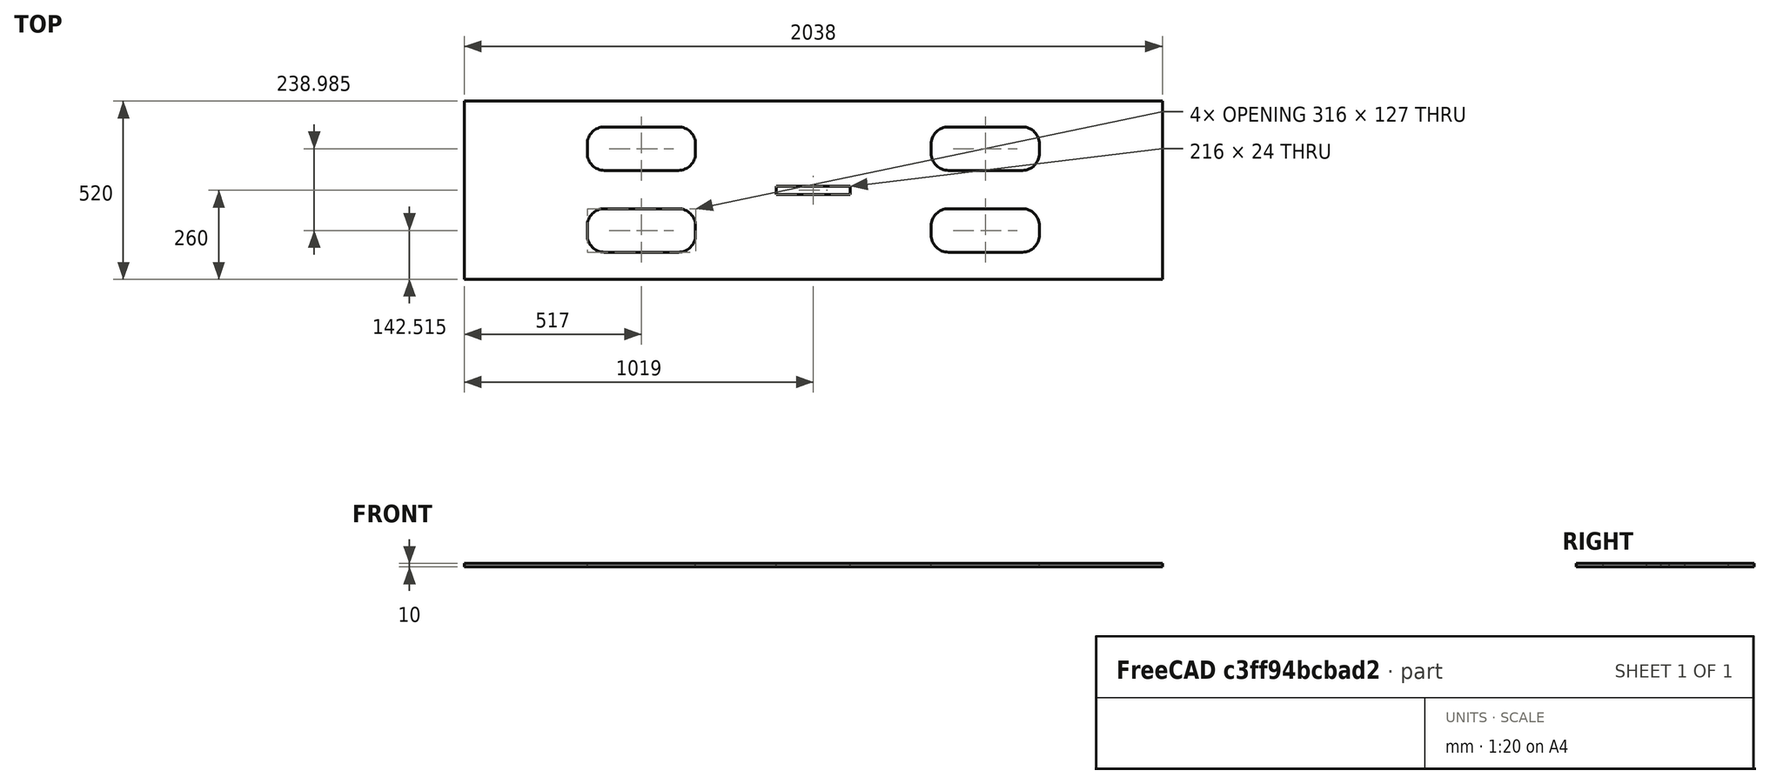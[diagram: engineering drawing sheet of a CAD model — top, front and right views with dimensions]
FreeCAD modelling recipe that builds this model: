
FCSTD DOCUMENT  (FreeCAD 1.0R39319 (Git))
Label: comp20_16mm_plate
License: All rights reserved
LicenseURL: https://en.wikipedia.org/wiki/All_rights_reserved
objects: Sketcher::SketchObject×1, PartDesign::Pad×1, PartDesign::Body×1
note: 6 computed .brp shape members not serialized (recipe doc carries the construction recipe); baked Part::Feature solids carry a one-line shape summary decoded from their .brp

FEATURE [Sketcher::SketchObject] Sketch
  ArcFitTolerance = 1e-06
  AttachmentSupport = -> [XY_Plane]
  FullyConstrained = true
  MakeInternals = false
  MapMode = 5
  sketch-geometry (50):
    g0: LineSegment StartX=0 StartY=0 StartZ=0 EndX=2038 EndY=0 EndZ=0
    g1: LineSegment StartX=2038 StartY=0 StartZ=0 EndX=2038 EndY=520 EndZ=0
    g2: LineSegment StartX=2038 StartY=520 StartZ=0 EndX=0 EndY=520 EndZ=0
    g3: LineSegment StartX=0 StartY=520 StartZ=0 EndX=0 EndY=0 EndZ=0
    g4: LineSegment StartX=359 StartY=395 StartZ=0 EndX=359 EndY=368 EndZ=0
    g5: LineSegment StartX=409 StartY=318 StartZ=0 EndX=625 EndY=318 EndZ=0
    g6: LineSegment StartX=675 StartY=368 StartZ=0 EndX=675 EndY=395 EndZ=0
    g7: LineSegment StartX=625 StartY=445 StartZ=0 EndX=409 EndY=445 EndZ=0
    g8: ArcOfCircle CenterX=409 CenterY=395 CenterZ=0 NormalX=0 NormalY=0 NormalZ=1 AngleXU=0 Radius=50 StartAngle=1.5708 EndAngle=3.14159
    g9: ArcOfCircle CenterX=409 CenterY=368 CenterZ=0 NormalX=0 NormalY=0 NormalZ=1 AngleXU=0 Radius=50 StartAngle=3.14159 EndAngle=4.71239
    g10: ArcOfCircle CenterX=625 CenterY=368 CenterZ=0 NormalX=0 NormalY=0 NormalZ=1 AngleXU=0 Radius=50 StartAngle=4.71239 EndAngle=6.28319
    g11: ArcOfCircle CenterX=625 CenterY=395 CenterZ=0 NormalX=0 NormalY=0 NormalZ=1 AngleXU=0 Radius=50 StartAngle=-1.33e-14 EndAngle=1.5708
    g12: GeomPoint [constr] X=359 Y=445 Z=0
    g13: GeomPoint [constr] X=675 Y=318 Z=0
    g14: LineSegment StartX=1363 StartY=395 StartZ=0 EndX=1363 EndY=368 EndZ=0
    g15: LineSegment StartX=1413 StartY=318 StartZ=0 EndX=1629 EndY=318 EndZ=0
    g16: LineSegment StartX=1679 StartY=368 StartZ=0 EndX=1679 EndY=395 EndZ=0
    g17: LineSegment StartX=1629 StartY=445 StartZ=0 EndX=1413 EndY=445 EndZ=0
    g18: ArcOfCircle CenterX=1413 CenterY=395 CenterZ=0 NormalX=0 NormalY=0 NormalZ=1 AngleXU=0 Radius=50 StartAngle=1.5708 EndAngle=3.14159
    g19: ArcOfCircle CenterX=1413 CenterY=368 CenterZ=0 NormalX=0 NormalY=0 NormalZ=1 AngleXU=0 Radius=50 StartAngle=3.14159 EndAngle=4.71239
    g20: ArcOfCircle CenterX=1629 CenterY=368 CenterZ=0 NormalX=0 NormalY=0 NormalZ=1 AngleXU=0 Radius=50 StartAngle=4.71239 EndAngle=6.28319
    g21: ArcOfCircle CenterX=1629 CenterY=395 CenterZ=0 NormalX=0 NormalY=0 NormalZ=1 AngleXU=0 Radius=50 StartAngle=-1.42e-14 EndAngle=1.5708
    g22: GeomPoint [constr] X=1363 Y=445 Z=0
    g23: GeomPoint [constr] X=1679 Y=318 Z=0
    g24: LineSegment StartX=359 StartY=156.015 StartZ=0 EndX=359 EndY=129.015 EndZ=0
    g25: LineSegment StartX=409 StartY=79.0146 StartZ=0 EndX=625 EndY=79.0146 EndZ=0
    g26: LineSegment StartX=675 StartY=129.015 StartZ=0 EndX=675 EndY=156.015 EndZ=0
    g27: LineSegment StartX=625 StartY=206.015 StartZ=0 EndX=409 EndY=206.015 EndZ=0
    g28: ArcOfCircle CenterX=409 CenterY=156.015 CenterZ=0 NormalX=0 NormalY=0 NormalZ=1 AngleXU=0 Radius=50 StartAngle=1.5708 EndAngle=3.14159
    g29: ArcOfCircle CenterX=409 CenterY=129.015 CenterZ=0 NormalX=0 NormalY=0 NormalZ=1 AngleXU=0 Radius=50 StartAngle=3.14159 EndAngle=4.71239
    g30: ArcOfCircle CenterX=625 CenterY=129.015 CenterZ=0 NormalX=0 NormalY=0 NormalZ=1 AngleXU=0 Radius=50 StartAngle=4.71239 EndAngle=6.28319
    g31: ArcOfCircle CenterX=625 CenterY=156.015 CenterZ=0 NormalX=0 NormalY=0 NormalZ=1 AngleXU=0 Radius=50 StartAngle=1e-16 EndAngle=1.5708
    g32: GeomPoint [constr] X=359 Y=206.015 Z=0
    g33: GeomPoint [constr] X=675 Y=79.0146 Z=0
    g34: LineSegment StartX=1363 StartY=156.015 StartZ=0 EndX=1363 EndY=129.015 EndZ=0
    g35: LineSegment StartX=1413 StartY=79.0146 StartZ=0 EndX=1629 EndY=79.0146 EndZ=0
    g36: LineSegment StartX=1679 StartY=129.015 StartZ=0 EndX=1679 EndY=156.015 EndZ=0
    g37: LineSegment StartX=1629 StartY=206.015 StartZ=0 EndX=1413 EndY=206.015 EndZ=0
    g38: ArcOfCircle CenterX=1413 CenterY=156.015 CenterZ=0 NormalX=0 NormalY=0 NormalZ=1 AngleXU=0 Radius=50 StartAngle=1.5708 EndAngle=3.14159
    g39: ArcOfCircle CenterX=1413 CenterY=129.015 CenterZ=0 NormalX=0 NormalY=0 NormalZ=1 AngleXU=0 Radius=50 StartAngle=3.14159 EndAngle=4.71239
    g40: ArcOfCircle CenterX=1629 CenterY=129.015 CenterZ=0 NormalX=0 NormalY=0 NormalZ=1 AngleXU=0 Radius=50 StartAngle=4.71239 EndAngle=6.28319
    g41: ArcOfCircle CenterX=1629 CenterY=156.015 CenterZ=0 NormalX=0 NormalY=0 NormalZ=1 AngleXU=0 Radius=50 StartAngle=0 EndAngle=1.5708
    g42: GeomPoint [constr] X=1363 Y=206.015 Z=0
    g43: GeomPoint [constr] X=1679 Y=79.0146 Z=0
    g44: LineSegment StartX=911 StartY=272 StartZ=0 EndX=911 EndY=248 EndZ=0
    g45: LineSegment StartX=911 StartY=248 StartZ=0 EndX=1127 EndY=248 EndZ=0
    g46: LineSegment StartX=1127 StartY=248 StartZ=0 EndX=1127 EndY=272 EndZ=0
    g47: LineSegment StartX=1127 StartY=272 StartZ=0 EndX=911 EndY=272 EndZ=0
    g48: LineSegment [constr] StartX=1019 StartY=520 StartZ=0 EndX=1019 EndY=272 EndZ=0
    g49: LineSegment [constr] StartX=1019 StartY=248 StartZ=0 EndX=1019 EndY=0 EndZ=0
  constraints (123):
    c: Coincident(g0,g1)
    c: Coincident(g1,g2)
    c: Coincident(g2,g3)
    c: Coincident(g3,g0)
    c: Horizontal(g0)
    c: Horizontal(g2)
    c: Vertical(g1)
    c: Vertical(g3)
    c: Coincident(g0,g-1)
    c: DistanceX(g2,g2) = 2038
    c: DistanceY(g1,g1) = 520
    c: Tangent(g4,g8) = -1.5708
    c: Tangent(g4,g9) = -1.5708
    c: Tangent(g5,g9) = -1.5708
    c: Tangent(g5,g10) = -1.5708
    c: Tangent(g6,g10) = -1.5708
    c: Tangent(g6,g11) = -1.5708
    c: Tangent(g7,g11) = -1.5708
    c: Tangent(g7,g8) = -1.5708
    c: Vertical(g4)
    c: Vertical(g6)
    c: Horizontal(g5)
    c: Horizontal(g7)
    c: Equal(g8,g9)
    c: Equal(g9,g10)
    c: Equal(g10,g11)
    c: PointOnObject(g12,g4)
    c: PointOnObject(g12,g7)
    c: PointOnObject(g13,g5)
    c: PointOnObject(g13,g6)
    c: Tangent(g14,g18) = -1.5708
    c: Tangent(g14,g19) = -1.5708
    c: Tangent(g15,g19) = -1.5708
    c: Tangent(g15,g20) = -1.5708
    c: Tangent(g16,g20) = -1.5708
    c: Tangent(g16,g21) = -1.5708
    c: Tangent(g17,g21) = -1.5708
    c: Tangent(g17,g18) = -1.5708
    c: Vertical(g14)
    c: Vertical(g16)
    c: Horizontal(g15)
    c: Horizontal(g17)
    c: Equal(g18,g19)
    c: Equal(g19,g20)
    c: Equal(g20,g21)
    c: PointOnObject(g22,g14)
    c: PointOnObject(g22,g17)
    c: PointOnObject(g23,g15)
    c: PointOnObject(g23,g16)
    c: Tangent(g24,g28) = -1.5708
    c: Tangent(g24,g29) = -1.5708
    c: Tangent(g25,g29) = -1.5708
    c: Tangent(g25,g30) = -1.5708
    c: Tangent(g26,g30) = -1.5708
    c: Tangent(g26,g31) = -1.5708
    c: Tangent(g27,g31) = -1.5708
    c: Tangent(g27,g28) = -1.5708
    c: Vertical(g24)
    c: Vertical(g26)
    c: Horizontal(g25)
    c: Horizontal(g27)
    c: Equal(g28,g29)
    c: Equal(g29,g30)
    c: Equal(g30,g31)
    c: PointOnObject(g32,g24)
    c: PointOnObject(g32,g27)
    c: PointOnObject(g33,g25)
    c: PointOnObject(g33,g26)
    c: DistanceX(g7,g7) = 216
    c: Radius(g8) = 50
    c: DistanceY(g6,g6) = 27
    c: Equal(g7,g27)
    c: Equal(g27,g17)
    c: Equal(g8,g28)
    c: Equal(g28,g18)
    c: Equal(g6,g14)
    c: Equal(g14,g26)
    c: Tangent(g34,g38) = -1.5708
    c: Tangent(g34,g39) = -1.5708
    c: Tangent(g35,g39) = -1.5708
    c: Tangent(g35,g40) = -1.5708
    c: Tangent(g36,g40) = -1.5708
    c: Tangent(g36,g41) = -1.5708
    c: Tangent(g37,g41) = -1.5708
    c: Tangent(g37,g38) = -1.5708
    c: Vertical(g34)
    c: Vertical(g36)
    c: Horizontal(g35)
    c: Horizontal(g37)
    c: Equal(g38,g39)
    c: Equal(g39,g40)
    c: Equal(g40,g41)
    c: PointOnObject(g42,g34)
    c: PointOnObject(g42,g37)
    c: PointOnObject(g43,g35)
    c: PointOnObject(g43,g36)
    c: Equal(g7,g37)
    c: Equal(g6,g34)
    c: Equal(g11,g38)
    c: Distance(g29,g3) = 409
    c: Distance(g16,g1) = 359
    c: Distance(g16,g2) = 125
    c: Distance(g6,g14) = 688
    c: Distance(g6,g2) = 125
    c: Distance(g34,g0) = 129.015
    c: Horizontal(g32,g42)
    c: Vertical(g23,g43)
    c: Coincident(g44,g45)
    c: Coincident(g45,g46)
    c: Coincident(g46,g47)
    c: Coincident(g47,g44)
    c: Vertical(g44)
    c: Vertical(g46)
    c: Horizontal(g45)
    c: Horizontal(g47)
    c: Distance(g44,g44) = 24
    c: DistanceX(g47,g47) = 216
    c: Distance(g3,g44) = 911
    c: Symmetric(g2,g2,g48)
    c: Symmetric(g47,g47,g48)
    c: Symmetric(g45,g45,g49)
    c: Symmetric(g0,g0,g49)
    c: Equal(g48,g49)
FEATURE [PartDesign::Pad] Pad
  Direction = (0,0,1)
  Length = 10
  Length2 = 10
  Profile = -> Sketch
  ReferenceAxis = -> Sketch [N_Axis]
  Refine = true
  Suppressed = false
  Type = 0
FEATURE [PartDesign::Body] Body
  AllowCompound = false
  Group = -> [Sketch,Pad]
  Origin = -> Origin
  Tip = -> Pad
